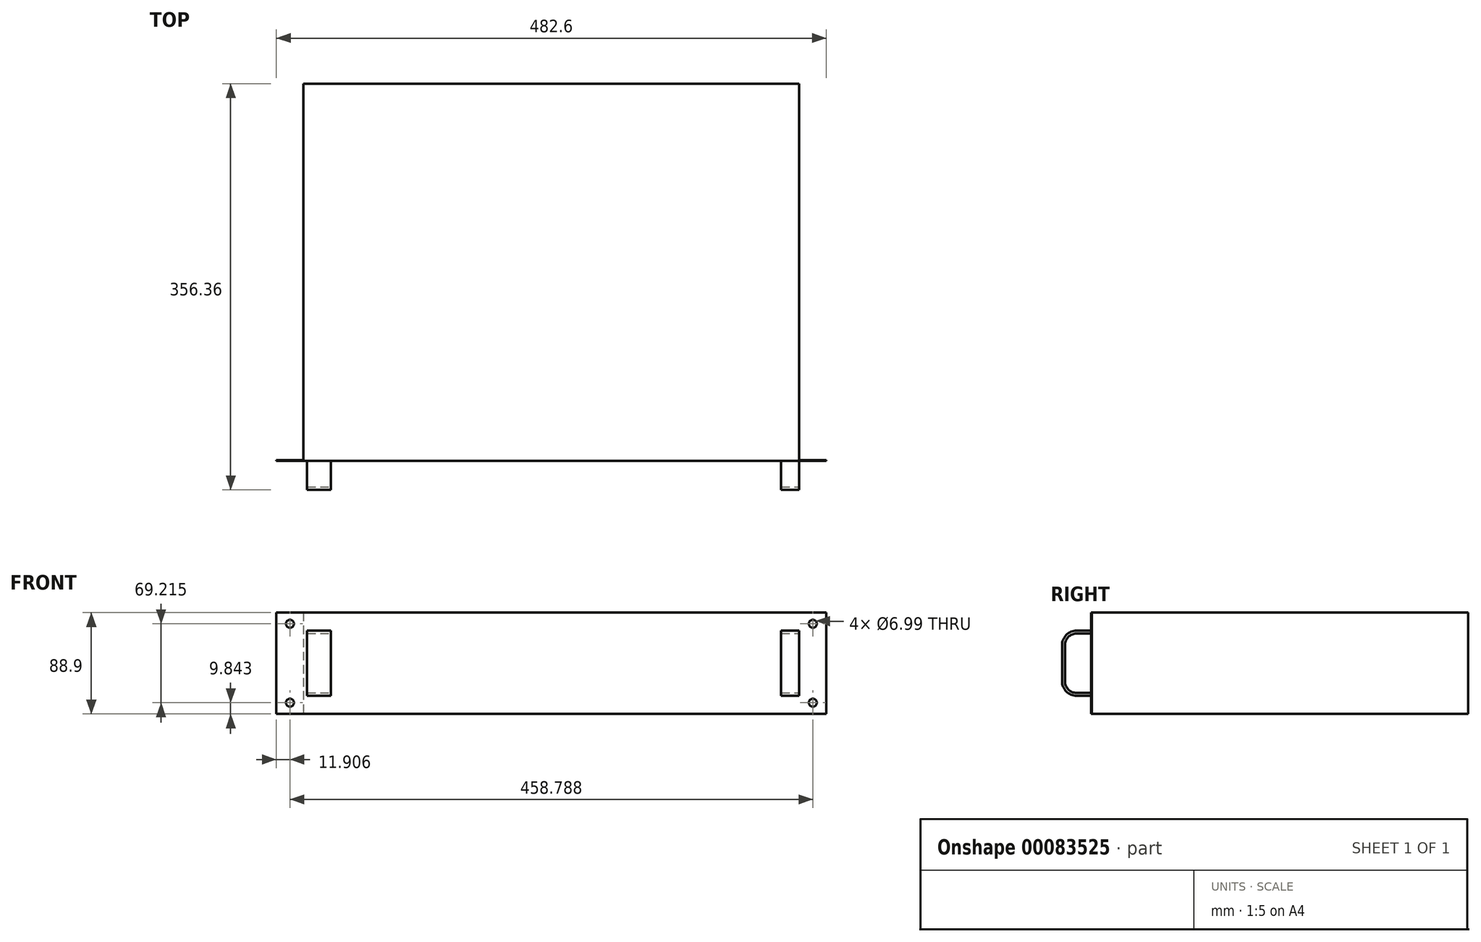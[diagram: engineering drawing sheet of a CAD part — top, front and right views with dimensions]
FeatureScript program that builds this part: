
annotation { "Feature Type Name" : "Feature", "Feature Type Description" : "" }
export const myFeature = defineFeature(function(context is Context, id is Id, definition is map)
    precondition{}
    {
        {
            var Q0;
            Q0=qCreatedBy(makeId("Top.planeOp"),FACE);
            var sketch = newSketch(context, id + "F0", { "sketchPlane" : qUnion([Q0])});
            skLineSegment(sketch, "E0.bottom", {"start": v(-217.49, 165.1) * mm, "end": v(217.49, 165.1) * mm});
            skLineSegment(sketch, "E0.top", {"start": v(-217.49, -165.1) * mm, "end": v(217.49, -165.1) * mm});
            skLineSegment(sketch, "E0.left", {"start": v(-217.49, 165.1) * mm, "end": v(-217.49, -165.1) * mm});
            skLineSegment(sketch, "E0.right", {"start": v(217.49, 165.1) * mm, "end": v(217.49, -165.1) * mm});
            skPoint(sketch, "E0.middle", {"position": v(0, 0) * mm});
            skSolve(sketch);
        }
        {
            var Q0;
            Q0 = qSketchRegion(id + "F0", true);
            extrude(context, id + "F1", {"entities" : qUnion([Q0]), "endBound" : BoundingType.SYMMETRIC, "depth" : 88.9 * mm});
        }
        {
            var Q0;
            Q0=makeQuery(id+"F1.opExtrude","SWEPT_FACE",FACE,{"disambiguationData":[OSD([sQuery(id+"F0.wireOp",EDGE,"E0.top")])]});
            var sketch = newSketch(context, id + "F2", { "sketchPlane" : qUnion([Q0])});
            skLineSegment(sketch, "E1.bottom", {"start": v(-241.3, -44.45) * mm, "end": v(241.3, -44.45) * mm});
            skLineSegment(sketch, "E1.top", {"start": v(-241.3, 44.45) * mm, "end": v(241.3, 44.45) * mm});
            skLineSegment(sketch, "E1.left", {"start": v(-241.3, -44.45) * mm, "end": v(-241.3, 44.45) * mm});
            skLineSegment(sketch, "E1.right", {"start": v(241.3, -44.45) * mm, "end": v(241.3, 44.45) * mm});
            skLineSegment(sketch, "E2", {"start": v(-241.3, -44.45) * mm, "end": v(-217.49, -44.45) * mm});
            skLineSegment(sketch, "E3", {"start": v(-229.4, -44.45) * mm, "end": v(-229.4, 44.45) * mm, "construction": true});
            skLineSegment(sketch, "E4", {"start": v(-241.3, 0) * mm, "end": v(-217.49, 0) * mm, "construction": true});
            skCircle(sketch, "E5", {"center": v(-229.4, 34.6) * mm, "radius": 3.5 * mm});
            skCircle(sketch, "E6.MirrorC", {"center": v(-229.4, -34.6) * mm, "radius": 3.5 * mm});
            skLineSegment(sketch, "E7", {"start": v(0, -44.45) * mm, "end": v(0, 44.45) * mm, "construction": true});
            skLineSegment(sketch, "E8.MirrorCS", {"start": v(229.4, -44.45) * mm, "end": v(229.4, 44.45) * mm, "construction": true});
            skCircle(sketch, "E9.MirrorC", {"center": v(229.4, 34.6) * mm, "radius": 3.5 * mm});
            skCircle(sketch, "E10.MirrorC", {"center": v(229.4, -34.6) * mm, "radius": 3.5 * mm});
            skSolve(sketch);
        }
        {
            var Q0;
            Q0 = qSketchRegion(id + "F2", true);
            extrude(context, id + "F3", {"entities" : qUnion([Q0]), "operationType" : NewBodyOperationType.ADD, "depth" : 0.76 * mm});
        }
        {
            var Q0;
            Q0=makeQuery(id+"F1.opExtrude","SWEPT_FACE",FACE,{"disambiguationData":[OSD([sQuery(id+"F0.wireOp",EDGE,"E0.right")])]});
            var sketch = newSketch(context, id + "F4", { "sketchPlane" : qUnion([Q0])});
            skLineSegment(sketch, "E11", {"start": v(-165.1, 0) * mm, "end": v(165.1, 0) * mm, "construction": true});
            skLineSegment(sketch, "E12", {"start": v(-165.1, 44.45) * mm, "end": v(-165.86, 44.45) * mm, "construction": true});
            skLineSegment(sketch, "E13", {"start": v(-165.86, 44.45) * mm, "end": v(-165.86, 0) * mm, "construction": true});
            skLineSegment(sketch, "E14", {"start": v(-165.86, 0) * mm, "end": v(-191.26, 0) * mm, "construction": true});
            skLineSegment(sketch, "E15", {"start": v(-191.26, 0) * mm, "end": v(-191.26, 15.88) * mm});
            skLineSegment(sketch, "E16", {"start": v(-178.56, 28.58) * mm, "end": v(-165.86, 28.58) * mm});
            skPoint(sketch, "E17.visualSharp", {"position": v(-191.26, 28.58) * mm});
            skArc(sketch, "E17.filletArc", {"start": v(-178.56, 28.58) * mm, "mid": v(-187.54, 24.86) * mm, "end": v(-191.26, 15.88) * mm});
            skLineSegment(sketch, "E18.0", {"start": v(-178.56, 26.04) * mm, "end": v(-165.86, 26.04) * mm});
            skArc(sketch, "E18.1", {"start": v(-178.56, 26.04) * mm, "mid": v(-185.75, 23.06) * mm, "end": v(-188.72, 15.88) * mm});
            skLineSegment(sketch, "E18.2", {"start": v(-188.72, 0) * mm, "end": v(-188.72, 15.88) * mm});
            skLineSegment(sketch, "E19", {"start": v(-165.86, 28.58) * mm, "end": v(-165.86, 26.04) * mm});
            skPoint(sketch, "E20.MirrorP", {"position": v(-191.26, -28.58) * mm});
            skLineSegment(sketch, "E21.MirrorCS", {"start": v(-178.56, -26.04) * mm, "end": v(-165.86, -26.04) * mm});
            skLineSegment(sketch, "E22.MirrorCS", {"start": v(-188.72, 0) * mm, "end": v(-188.72, -15.88) * mm});
            skLineSegment(sketch, "E23.MirrorCS", {"start": v(-178.56, -28.58) * mm, "end": v(-165.86, -28.58) * mm});
            skLineSegment(sketch, "E24.MirrorCS", {"start": v(-191.26, 0) * mm, "end": v(-191.26, -15.88) * mm});
            skArc(sketch, "E25.MirrorCS", {"start": v(-178.56, -26.04) * mm, "mid": v(-185.75, -23.06) * mm, "end": v(-188.72, -15.88) * mm});
            skArc(sketch, "E26.MirrorCS", {"start": v(-178.56, -28.58) * mm, "mid": v(-187.54, -24.86) * mm, "end": v(-191.26, -15.88) * mm});
            skLineSegment(sketch, "E27", {"start": v(-165.86, -28.58) * mm, "end": v(-165.86, -26.04) * mm});
            skSolve(sketch);
        }
        {
            var Q0;
            Q0 = qSketchRegion(id + "F4", true);
            extrude(context, id + "F5", {"entities" : qUnion([Q0]), "operationType" : NewBodyOperationType.ADD, "oppositeDirection" : true, "depth" : 431.8 * mm});
        }
        {
            var Q0;
            Q0=makeQuery(id+"F3.boolean.opBoolean","MERGE",FACE,{"derivedFrom":[makeQuery(id+"F1.opExtrude","CAP_FACE",FACE,{"disambiguationData":[OSD([sQuery(id+"F0.wireOp",EDGE,"E0.bottom"),sQuery(id+"F0.wireOp",EDGE,"E0.top"),sQuery(id+"F0.wireOp",EDGE,"E0.left"),sQuery(id+"F0.wireOp",EDGE,"E0.right")])],"isStart":false}),makeQuery(id+"F3.opExtrude","SWEPT_FACE",FACE,{"disambiguationData":[OSD([sQuery(id+"F2.wireOp",EDGE,"E1.top")])]})]});
            var sketch = newSketch(context, id + "F6", { "sketchPlane" : qUnion([Q0])});
            skLineSegment(sketch, "E28", {"start": v(0, 0) * mm, "end": v(0, -165.86) * mm, "construction": true});
            skLineSegment(sketch, "E29", {"start": v(-193.41, -165.86) * mm, "end": v(201.61, -165.86) * mm});
            skLineSegment(sketch, "E30", {"start": v(201.61, -165.86) * mm, "end": v(201.61, -191.26) * mm});
            skLineSegment(sketch, "E31", {"start": v(201.61, -191.26) * mm, "end": v(-193.41, -191.26) * mm});
            skLineSegment(sketch, "E32", {"start": v(-193.41, -191.26) * mm, "end": v(-193.41, -165.86) * mm});
            skSolve(sketch);
        }
        {
            var Q0;
            Q0 = qSketchRegion(id + "F6", true);
            extrude(context, id + "F7", {"entities" : qUnion([Q0]), "operationType" : NewBodyOperationType.REMOVE, "endBound" : BoundingType.THROUGH_ALL, "oppositeDirection" : true, "depth" : 25.4 * mm});
        }
    });
